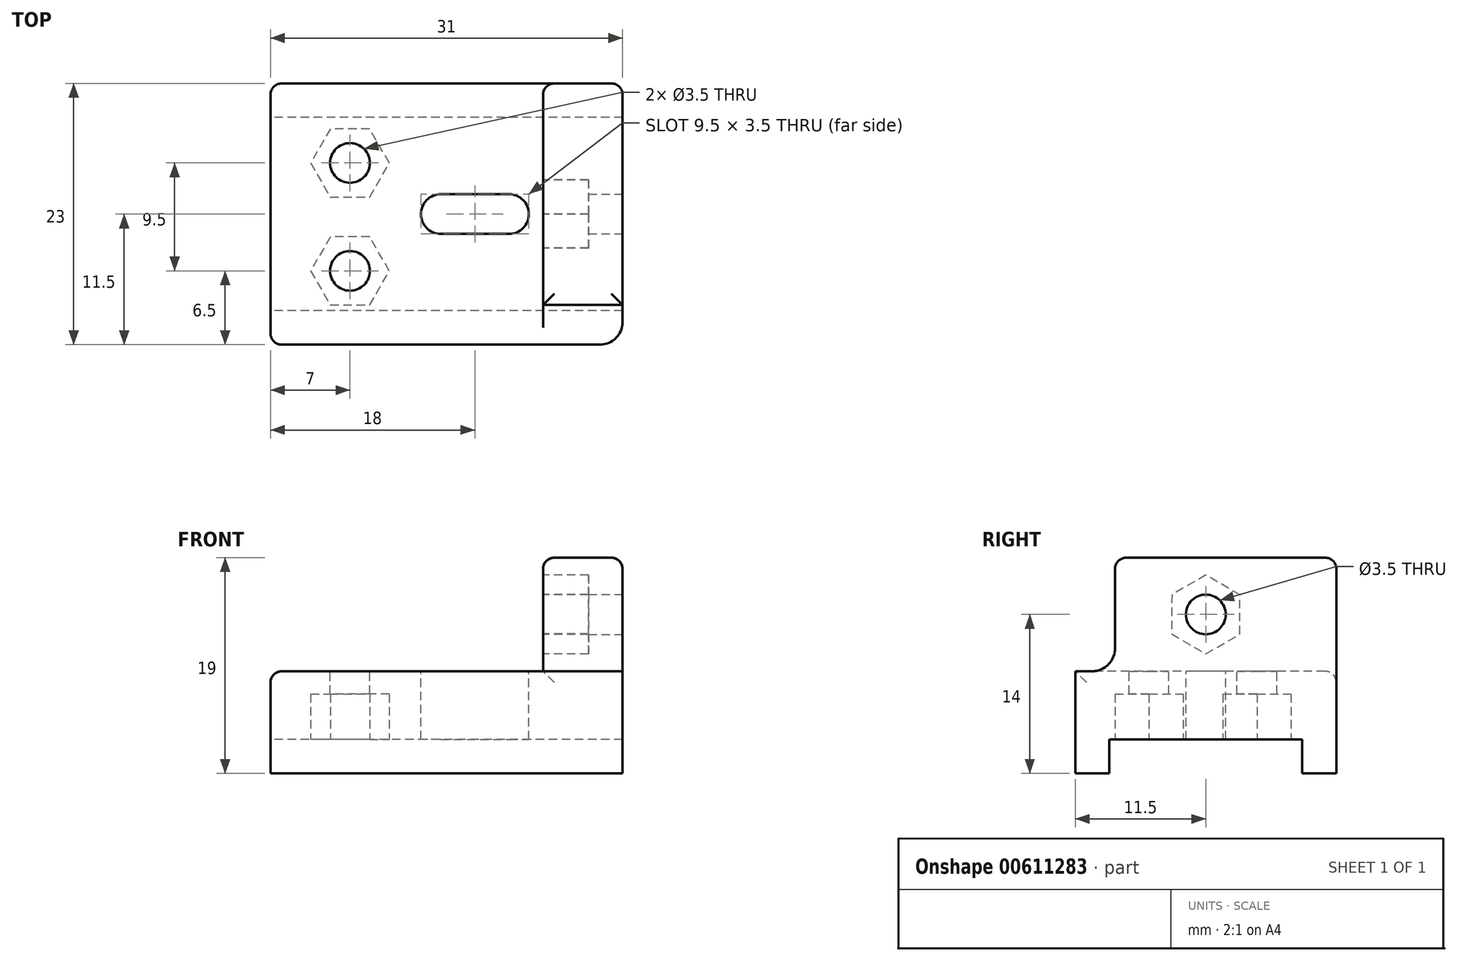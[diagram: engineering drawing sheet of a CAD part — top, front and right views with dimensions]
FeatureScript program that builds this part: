
annotation { "Feature Type Name" : "Feature", "Feature Type Description" : "" }
export const myFeature = defineFeature(function(context is Context, id is Id, definition is map)
    precondition{}
    {
        {
            var Q0;
            Q0=qCreatedBy(makeId("Top.planeOp"),FACE);
            var sketch = newSketch(context, id + "F0", { "sketchPlane" : qUnion([Q0])});
            skLineSegment(sketch, "E0.bottom", {"start": v(0, 0) * mm, "end": v(14, 0) * mm});
            skLineSegment(sketch, "E0.top", {"start": v(0, -23) * mm, "end": v(14, -23) * mm});
            skLineSegment(sketch, "E0.left", {"start": v(0, 0) * mm, "end": v(0, -23) * mm});
            skLineSegment(sketch, "E0.right", {"start": v(14, 0) * mm, "end": v(14, -23) * mm});
            skLineSegment(sketch, "E1.bottom", {"start": v(0, -7) * mm, "end": v(14, -7) * mm, "construction": true});
            skLineSegment(sketch, "E1.top", {"start": v(0, -16.5) * mm, "end": v(14, -16.5) * mm, "construction": true});
            skLineSegment(sketch, "E1.left", {"start": v(0, -7) * mm, "end": v(0, -16.5) * mm, "construction": true});
            skLineSegment(sketch, "E1.right", {"start": v(14, -7) * mm, "end": v(14, -16.5) * mm, "construction": true});
            skCircle(sketch, "E2", {"center": v(7, -7) * mm, "radius": 1.75 * mm});
            skCircle(sketch, "E3", {"center": v(7, -16.5) * mm, "radius": 1.75 * mm});
            skSolve(sketch);
        }
        {
            var Q0;
            Q0=makeQuery(id+"F0.imprint","IMPRINT",FACE,{"disambiguationData":[TD([[makeQuery(id+"F0.imprint","IMPRINT",EDGE,{"derivedFrom":sQuery(id+"F0.wireOp",EDGE,"E0.bottom")}),-1.0]])]});
            var Q1;
            Q1=makeQuery(id+"F0.imprint","IMPRINT",FACE,{"disambiguationData":[TD([[makeQuery(id+"F0.imprint","IMPRINT",EDGE,{"derivedFrom":sQuery(id+"F0.wireOp",EDGE,"E2")}),1.0]])]});
            var Q2;
            Q2=makeQuery(id+"F0.imprint","IMPRINT",FACE,{"disambiguationData":[TD([[makeQuery(id+"F0.imprint","IMPRINT",EDGE,{"derivedFrom":sQuery(id+"F0.wireOp",EDGE,"E3")}),1.0]])]});
            extrude(context, id + "F1", {"entities" : qUnion([Q0, Q1, Q2]), "depth" : 6 * mm, "offsetDistance" : 25 * mm});
        }
        {
            var Q0;
            Q0=makeQuery(id+"F1.opExtrude","CAP_FACE",FACE,{"disambiguationData":[OSD([sQuery(id+"F0.wireOp",EDGE,"E0.bottom"),sQuery(id+"F0.wireOp",EDGE,"E0.top"),sQuery(id+"F0.wireOp",EDGE,"E0.left"),sQuery(id+"F0.wireOp",EDGE,"E0.right")])],"isStart":true});
            var sketch = newSketch(context, id + "F2", { "sketchPlane" : qUnion([Q0])});
            skLineSegment(sketch, "E4.bottom", {"start": v(14, 7) * mm, "end": v(0, 7) * mm, "construction": true});
            skLineSegment(sketch, "E4.top", {"start": v(14, 16.5) * mm, "end": v(0, 16.5) * mm, "construction": true});
            skLineSegment(sketch, "E4.left", {"start": v(14, 7) * mm, "end": v(14, 16.5) * mm, "construction": true});
            skLineSegment(sketch, "E4.right", {"start": v(0, 7) * mm, "end": v(0, 16.5) * mm, "construction": true});
            skCircle(sketch, "E5.cCircle", {"center": v(7, 7) * mm, "radius": 3 * mm, "construction": true});
            skLineSegment(sketch, "E5.0", {"start": v(8.73, 4) * mm, "end": v(5.27, 4) * mm});
            skLineSegment(sketch, "E5.1", {"start": v(5.27, 4) * mm, "end": v(3.54, 7) * mm});
            skLineSegment(sketch, "E5.2", {"start": v(3.54, 7) * mm, "end": v(5.27, 10) * mm});
            skLineSegment(sketch, "E5.3", {"start": v(5.27, 10) * mm, "end": v(8.73, 10) * mm});
            skLineSegment(sketch, "E5.4", {"start": v(8.73, 10) * mm, "end": v(10.46, 7) * mm});
            skLineSegment(sketch, "E5.5", {"start": v(10.46, 7) * mm, "end": v(8.73, 4) * mm});
            skPoint(sketch, "E5.0.midPoint", {"position": v(7, 4) * mm});
            skCircle(sketch, "E6.cCircle", {"center": v(7, 16.5) * mm, "radius": 3 * mm, "construction": true});
            skLineSegment(sketch, "E6.0", {"start": v(8.73, 13.5) * mm, "end": v(5.27, 13.5) * mm});
            skLineSegment(sketch, "E6.1", {"start": v(5.27, 13.5) * mm, "end": v(3.54, 16.5) * mm});
            skLineSegment(sketch, "E6.2", {"start": v(3.54, 16.5) * mm, "end": v(5.27, 19.5) * mm});
            skLineSegment(sketch, "E6.3", {"start": v(5.27, 19.5) * mm, "end": v(8.73, 19.5) * mm});
            skLineSegment(sketch, "E6.4", {"start": v(8.73, 19.5) * mm, "end": v(10.46, 16.5) * mm});
            skLineSegment(sketch, "E6.5", {"start": v(10.46, 16.5) * mm, "end": v(8.73, 13.5) * mm});
            skPoint(sketch, "E6.0.midPoint", {"position": v(7, 13.5) * mm});
            skSolve(sketch);
        }
        {
            var Q0;
            Q0=makeQuery(id+"F2.imprint","IMPRINT",FACE,{"disambiguationData":[TD([[makeQuery(id+"F2.imprint","IMPRINT",EDGE,{"derivedFrom":sQuery(id+"F2.wireOp",EDGE,"E5.0")}),-1.0]])]});
            var Q1;
            Q1=makeQuery(id+"F2.imprint","IMPRINT",FACE,{"disambiguationData":[TD([[makeQuery(id+"F2.imprint","IMPRINT",EDGE,{"derivedFrom":sQuery(id+"F2.wireOp",EDGE,"E6.0")}),-1.0]])]});
            extrude(context, id + "F3", {"entities" : qUnion([Q0, Q1]), "operationType" : NewBodyOperationType.REMOVE, "oppositeDirection" : true, "depth" : 4 * mm, "offsetDistance" : 25 * mm});
        }
        {
            var Q0;
            Q0=makeQuery(id+"F1.opExtrude","CAP_FACE",FACE,{"disambiguationData":[OSD([sQuery(id+"F0.wireOp",EDGE,"E0.bottom"),sQuery(id+"F0.wireOp",EDGE,"E0.top"),sQuery(id+"F0.wireOp",EDGE,"E0.left"),sQuery(id+"F0.wireOp",EDGE,"E0.right")])],"isStart":false});
            var sketch = newSketch(context, id + "F4", { "sketchPlane" : qUnion([Q0])});
            skLineSegment(sketch, "E7.bottom", {"start": v(0, -7) * mm, "end": v(14, -7) * mm, "construction": true});
            skLineSegment(sketch, "E7.top", {"start": v(0, -16.5) * mm, "end": v(14, -16.5) * mm, "construction": true});
            skLineSegment(sketch, "E7.left", {"start": v(0, -7) * mm, "end": v(0, -16.5) * mm, "construction": true});
            skLineSegment(sketch, "E7.right", {"start": v(14, -7) * mm, "end": v(14, -16.5) * mm, "construction": true});
            skCircle(sketch, "E8", {"center": v(7, -7) * mm, "radius": 1.75 * mm});
            skCircle(sketch, "E9", {"center": v(7, -16.5) * mm, "radius": 1.75 * mm});
            skSolve(sketch);
        }
        {
            var Q0;
            Q0=makeQuery(id+"F4.imprint","IMPRINT",FACE,{"disambiguationData":[TD([[makeQuery(id+"F4.imprint","IMPRINT",EDGE,{"derivedFrom":sQuery(id+"F4.wireOp",EDGE,"E8")}),1.0]])]});
            var Q1;
            Q1=makeQuery(id+"F4.imprint","IMPRINT",FACE,{"disambiguationData":[TD([[makeQuery(id+"F4.imprint","IMPRINT",EDGE,{"derivedFrom":sQuery(id+"F4.wireOp",EDGE,"E9")}),1.0]])]});
            extrude(context, id + "F5", {"entities" : qUnion([Q0, Q1]), "operationType" : NewBodyOperationType.REMOVE, "oppositeDirection" : true, "depth" : 25 * mm, "offsetDistance" : 25 * mm});
        }
        {
            var Q0;
            Q0=makeQuery(id+"F1.opExtrude","CAP_FACE",FACE,{"disambiguationData":[OSD([sQuery(id+"F0.wireOp",EDGE,"E0.bottom"),sQuery(id+"F0.wireOp",EDGE,"E0.top"),sQuery(id+"F0.wireOp",EDGE,"E0.left"),sQuery(id+"F0.wireOp",EDGE,"E0.right")])],"isStart":true});
            var sketch = newSketch(context, id + "F6", { "sketchPlane" : qUnion([Q0])});
            skLineSegment(sketch, "E10.bottom", {"start": v(14, 3) * mm, "end": v(0, 3) * mm});
            skLineSegment(sketch, "E10.top", {"start": v(14, 0) * mm, "end": v(0, 0) * mm});
            skLineSegment(sketch, "E10.left", {"start": v(14, 3) * mm, "end": v(14, 0) * mm});
            skLineSegment(sketch, "E10.right", {"start": v(0, 3) * mm, "end": v(0, 0) * mm});
            skLineSegment(sketch, "E11.bottom", {"start": v(14, 23) * mm, "end": v(0, 23) * mm});
            skLineSegment(sketch, "E11.top", {"start": v(14, 20) * mm, "end": v(0, 20) * mm});
            skLineSegment(sketch, "E11.left", {"start": v(14, 23) * mm, "end": v(14, 20) * mm});
            skLineSegment(sketch, "E11.right", {"start": v(0, 23) * mm, "end": v(0, 20) * mm});
            skSolve(sketch);
        }
        {
            var Q0;
            Q0=makeQuery(id+"F6.imprint","IMPRINT",FACE,{"disambiguationData":[TD([[makeQuery(id+"F6.imprint","IMPRINT",EDGE,{"derivedFrom":sQuery(id+"F6.wireOp",EDGE,"E10.bottom")}),1.0]])]});
            var Q1;
            Q1=makeQuery(id+"F6.imprint","IMPRINT",FACE,{"disambiguationData":[TD([[makeQuery(id+"F6.imprint","IMPRINT",EDGE,{"derivedFrom":sQuery(id+"F6.wireOp",EDGE,"E11.bottom")}),-1.0]])]});
            extrude(context, id + "F7", {"entities" : qUnion([Q0, Q1]), "operationType" : NewBodyOperationType.ADD, "depth" : 3 * mm, "offsetDistance" : 25 * mm});
        }
        {
            var Q0;
            Q0=makeQuery(id+"F7.boolean.opBoolean","MERGE",FACE,{"derivedFrom":[makeQuery(id+"F1.opExtrude","SWEPT_FACE",FACE,{"disambiguationData":[OSD([sQuery(id+"F0.wireOp",EDGE,"E0.right")])]}),makeQuery(id+"F7.opExtrude","SWEPT_FACE",FACE,{"disambiguationData":[OSD([sQuery(id+"F6.wireOp",EDGE,"E10.left")])]}),makeQuery(id+"F7.opExtrude","SWEPT_FACE",FACE,{"disambiguationData":[OSD([sQuery(id+"F6.wireOp",EDGE,"E11.left")])]})]});
            extrude(context, id + "F8", {"entities" : qUnion([Q0]), "operationType" : NewBodyOperationType.ADD, "depth" : 17 * mm, "offsetDistance" : 25 * mm});
        }
        {
            var Q0;
            {var subQ0=sQuery(id+"F0.wireOp",EDGE,"E0.right");Q0=makeQuery(id+"F8.boolean.opBoolean","MERGE",FACE,{"derivedFrom":[makeQuery(id+"F1.opExtrude","CAP_FACE",FACE,{"disambiguationData":[OSD([sQuery(id+"F0.wireOp",EDGE,"E0.bottom"),sQuery(id+"F0.wireOp",EDGE,"E0.top"),sQuery(id+"F0.wireOp",EDGE,"E0.left"),subQ0])],"isStart":false}),makeQuery(id+"F8.opExtrude","SWEPT_FACE",FACE,{"disambiguationData":[OSD([subQ0]),TDD([makeQuery(id+"F1.opExtrude","CAP_EDGE",EDGE,{"disambiguationData":[OSD([subQ0])],"isStart":false})])]})]});}
            var sketch = newSketch(context, id + "F9", { "sketchPlane" : qUnion([Q0])});
            skLineSegment(sketch, "E12.bottom", {"start": v(24, 0) * mm, "end": v(31, 0) * mm});
            skLineSegment(sketch, "E12.top", {"start": v(24, -23) * mm, "end": v(31, -23) * mm});
            skLineSegment(sketch, "E12.left", {"start": v(24, 0) * mm, "end": v(24, -23) * mm});
            skLineSegment(sketch, "E12.right", {"start": v(31, 0) * mm, "end": v(31, -23) * mm});
            skSolve(sketch);
        }
        {
            var Q0;
            Q0=makeQuery(id+"F9.imprint","IMPRINT",FACE,{"disambiguationData":[TD([[makeQuery(id+"F9.imprint","IMPRINT",EDGE,{"derivedFrom":sQuery(id+"F9.wireOp",EDGE,"E12.bottom")}),-1.0]])]});
            extrude(context, id + "F10", {"entities" : qUnion([Q0]), "operationType" : NewBodyOperationType.ADD, "depth" : 10 * mm, "offsetDistance" : 25 * mm});
        }
        {
            var Q0;
            Q0=makeQuery(id+"F10.opExtrude","SWEPT_FACE",FACE,{"disambiguationData":[OSD([sQuery(id+"F9.wireOp",EDGE,"E12.left")])]});
            var sketch = newSketch(context, id + "F11", { "sketchPlane" : qUnion([Q0])});
            skLineSegment(sketch, "E13", {"start": v(0, 11) * mm, "end": v(23, 11) * mm, "construction": true});
            skCircle(sketch, "E14.cCircle", {"center": v(11.5, 11) * mm, "radius": 3 * mm, "construction": true});
            skLineSegment(sketch, "E14.0", {"start": v(8.49, 12.71) * mm, "end": v(11.48, 14.46) * mm});
            skLineSegment(sketch, "E14.1", {"start": v(11.48, 14.46) * mm, "end": v(14.49, 12.75) * mm});
            skLineSegment(sketch, "E14.2", {"start": v(14.49, 12.75) * mm, "end": v(14.51, 9.29) * mm});
            skLineSegment(sketch, "E14.3", {"start": v(14.51, 9.29) * mm, "end": v(11.52, 7.54) * mm});
            skLineSegment(sketch, "E14.4", {"start": v(11.52, 7.54) * mm, "end": v(8.51, 9.25) * mm});
            skLineSegment(sketch, "E14.5", {"start": v(8.51, 9.25) * mm, "end": v(8.49, 12.71) * mm});
            skPoint(sketch, "E14.0.midPoint", {"position": v(9.98, 13.59) * mm});
            skSolve(sketch);
        }
        {
            var Q0;
            Q0=makeQuery(id+"F11.imprint","IMPRINT",FACE,{"disambiguationData":[TD([[makeQuery(id+"F11.imprint","IMPRINT",EDGE,{"derivedFrom":sQuery(id+"F11.wireOp",EDGE,"E14.0")}),-1.0]])]});
            extrude(context, id + "F12", {"entities" : qUnion([Q0]), "operationType" : NewBodyOperationType.REMOVE, "oppositeDirection" : true, "depth" : 4 * mm, "offsetDistance" : 25 * mm});
        }
        {
            var Q0;
            Q0=makeQuery(id+"F10.boolean.opBoolean","MERGE",FACE,{"derivedFrom":[makeQuery(id+"F8.opExtrude","CAP_FACE",FACE,{"disambiguationData":[OSD([sQuery(id+"F0.wireOp",EDGE,"E0.right"),sQuery(id+"F6.wireOp",EDGE,"E10.left"),sQuery(id+"F6.wireOp",EDGE,"E11.left")])],"isStart":false}),makeQuery(id+"F10.opExtrude","SWEPT_FACE",FACE,{"disambiguationData":[OSD([sQuery(id+"F9.wireOp",EDGE,"E12.right")])]})]});
            var sketch = newSketch(context, id + "F13", { "sketchPlane" : qUnion([Q0])});
            skLineSegment(sketch, "E15", {"start": v(0, 11) * mm, "end": v(-23, 11) * mm, "construction": true});
            skCircle(sketch, "E16", {"center": v(-11.5, 11) * mm, "radius": 1.75 * mm});
            skSolve(sketch);
        }
        {
            var Q0;
            Q0=makeQuery(id+"F13.imprint","IMPRINT",FACE,{"disambiguationData":[TD([[makeQuery(id+"F13.imprint","IMPRINT",EDGE,{"derivedFrom":sQuery(id+"F13.wireOp",EDGE,"E16")}),1.0]])]});
            extrude(context, id + "F14", {"entities" : qUnion([Q0]), "operationType" : NewBodyOperationType.REMOVE, "oppositeDirection" : true, "depth" : 25 * mm, "offsetDistance" : 25 * mm});
        }
        {
            var Q0;
            {var subQ0=sQuery(id+"F0.wireOp",EDGE,"E0.right");Q0=makeQuery(id+"F8.boolean.opBoolean","MERGE",FACE,{"derivedFrom":[makeQuery(id+"F1.opExtrude","CAP_FACE",FACE,{"disambiguationData":[OSD([sQuery(id+"F0.wireOp",EDGE,"E0.bottom"),sQuery(id+"F0.wireOp",EDGE,"E0.top"),sQuery(id+"F0.wireOp",EDGE,"E0.left"),subQ0])],"isStart":false}),makeQuery(id+"F8.opExtrude","SWEPT_FACE",FACE,{"disambiguationData":[OSD([subQ0]),TDD([makeQuery(id+"F1.opExtrude","CAP_EDGE",EDGE,{"disambiguationData":[OSD([subQ0])],"isStart":false})])]})]});}
            var sketch = newSketch(context, id + "F15", { "sketchPlane" : qUnion([Q0])});
            skLineSegment(sketch, "E17", {"start": v(21, 0) * mm, "end": v(21, -23) * mm, "construction": true});
            skCircle(sketch, "E18", {"center": v(21, -11.5) * mm, "radius": 1.75 * mm});
            skLineSegment(sketch, "E19", {"start": v(14, 0) * mm, "end": v(14, -23) * mm, "construction": true});
            skLineSegment(sketch, "E20", {"start": v(15, 0) * mm, "end": v(15, -23) * mm, "construction": true});
            skCircle(sketch, "E21", {"center": v(15, -11.5) * mm, "radius": 1.75 * mm});
            skLineSegment(sketch, "E22", {"start": v(15, -9.75) * mm, "end": v(21, -9.75) * mm});
            skLineSegment(sketch, "E23", {"start": v(15, -13.25) * mm, "end": v(21, -13.25) * mm});
            skSolve(sketch);
        }
        {
            var Q0;
            {var subQ0=sQuery(id+"F15.wireOp",EDGE,"E22");Q0=makeQuery(id+"F15.imprint","IMPRINT",FACE,{"disambiguationData":[TD([[makeQuery(id+"F15.imprint","IMPRINT",EDGE,{"derivedFrom":subQ0}),-1.0]])]});}
            var Q1;
            {var subQ0=sQuery(id+"F15.wireOp",EDGE,"E21");var subQ1=makeQuery(id+"F15.imprint","INTERSECT",VERTEX,{"derivedFrom":[subQ0,sQuery(id+"F15.wireOp",EDGE,"E22")]});Q1=makeQuery(id+"F15.imprint","IMPRINT",FACE,{"disambiguationData":[TD([[makeQuery(id+"F15.imprint","IMPRINT",EDGE,{"disambiguationData":[TD([[subQ1,-1.0]])],"derivedFrom":subQ0}),1.0]])]});}
            var Q2;
            {var subQ0=sQuery(id+"F15.wireOp",EDGE,"E18");var subQ1=makeQuery(id+"F15.imprint","INTERSECT",VERTEX,{"derivedFrom":[subQ0,sQuery(id+"F15.wireOp",EDGE,"E22")]});Q2=makeQuery(id+"F15.imprint","IMPRINT",FACE,{"disambiguationData":[TD([[makeQuery(id+"F15.imprint","IMPRINT",EDGE,{"disambiguationData":[TD([[subQ1,-1.0]])],"derivedFrom":subQ0}),1.0]])]});}
            extrude(context, id + "F16", {"entities" : qUnion([Q0, Q1, Q2]), "operationType" : NewBodyOperationType.REMOVE, "oppositeDirection" : true, "depth" : 25 * mm, "offsetDistance" : 25 * mm});
        }
        {
            var Q0;
            {var subQ0=sQuery(id+"F6.wireOp",EDGE,"E11.bottom");var subQ1=sQuery(id+"F0.wireOp",EDGE,"E0.top");Q0=makeQuery(id+"F10.boolean.opBoolean","MERGE",FACE,{"derivedFrom":[makeQuery(id+"F8.boolean.opBoolean","MERGE",FACE,{"derivedFrom":[makeQuery(id+"F7.boolean.opBoolean","MERGE",FACE,{"derivedFrom":[makeQuery(id+"F1.opExtrude","SWEPT_FACE",FACE,{"disambiguationData":[OSD([subQ1])]}),makeQuery(id+"F7.opExtrude","SWEPT_FACE",FACE,{"disambiguationData":[OSD([subQ0])]})]}),makeQuery(id+"F8.opExtrude","SWEPT_FACE",FACE,{"disambiguationData":[OSD([subQ1,sQuery(id+"F0.wireOp",EDGE,"E0.right"),subQ0,sQuery(id+"F6.wireOp",EDGE,"E11.left")])]})]}),makeQuery(id+"F10.opExtrude","SWEPT_FACE",FACE,{"disambiguationData":[OSD([sQuery(id+"F9.wireOp",EDGE,"E12.top")])]})]});}
            var sketch = newSketch(context, id + "F17", { "sketchPlane" : qUnion([Q0])});
            skLineSegment(sketch, "E24.bottom", {"start": v(24, 6) * mm, "end": v(31, 6) * mm});
            skLineSegment(sketch, "E24.top", {"start": v(24, 16) * mm, "end": v(31, 16) * mm});
            skLineSegment(sketch, "E24.left", {"start": v(24, 6) * mm, "end": v(24, 16) * mm});
            skLineSegment(sketch, "E24.right", {"start": v(31, 6) * mm, "end": v(31, 16) * mm});
            skSolve(sketch);
        }
        {
            var Q0;
            Q0=makeQuery(id+"F17.imprint","IMPRINT",FACE,{"disambiguationData":[TD([[makeQuery(id+"F17.imprint","IMPRINT",EDGE,{"derivedFrom":sQuery(id+"F17.wireOp",EDGE,"E24.bottom")}),1.0]])]});
            extrude(context, id + "F18", {"entities" : qUnion([Q0]), "operationType" : NewBodyOperationType.REMOVE, "oppositeDirection" : true, "depth" : 3.5 * mm, "offsetDistance" : 25 * mm});
        }
        {
            var Q0;
            Q0=makeQuery(id+"F10.boolean.opBoolean","MERGE",EDGE,{"derivedFrom":[makeQuery(id+"F8.opExtrude","CAP_EDGE",EDGE,{"disambiguationData":[OSD([sQuery(id+"F0.wireOp",EDGE,"E0.top"),sQuery(id+"F0.wireOp",EDGE,"E0.right"),sQuery(id+"F6.wireOp",EDGE,"E11.bottom"),sQuery(id+"F6.wireOp",EDGE,"E11.left")])],"isStart":false}),makeQuery(id+"F10.opExtrude","SWEPT_EDGE",EDGE,{"disambiguationData":[OSD([sQuery(id+"F9.wireOp",EDGE,"E12.top"),sQuery(id+"F9.wireOp",EDGE,"E12.right")])]})]});
            fillet(context, id + "F19", {"entities" : qUnion([Q0]), "radius" : 2 * mm, "tangentPropagation" : true, "allowEdgeOverflow" : false});
        }
        {
            var Q0;
            Q0=makeQuery(id+"F18.boolean.opBoolean","COPY",EDGE,{"derivedFrom":makeQuery(id+"F18.opExtrude","CAP_EDGE",EDGE,{"disambiguationData":[OSD([sQuery(id+"F17.wireOp",EDGE,"E24.bottom")])],"isStart":false})});
            fillet(context, id + "F20", {"entities" : qUnion([Q0]), "radius" : 2 * mm, "tangentPropagation" : true, "allowEdgeOverflow" : false});
        }
        {
            var Q0;
            Q0=makeQuery(id+"F10.opExtrude","CAP_FACE",FACE,{"disambiguationData":[OSD([sQuery(id+"F9.wireOp",EDGE,"E12.bottom"),sQuery(id+"F9.wireOp",EDGE,"E12.top"),sQuery(id+"F9.wireOp",EDGE,"E12.left"),sQuery(id+"F9.wireOp",EDGE,"E12.right")])],"isStart":false});
            var Q1;
            Q1=makeQuery(id+"F10.boolean.opBoolean","MERGE",EDGE,{"derivedFrom":[makeQuery(id+"F8.opExtrude","CAP_EDGE",EDGE,{"disambiguationData":[OSD([sQuery(id+"F0.wireOp",EDGE,"E0.bottom"),sQuery(id+"F0.wireOp",EDGE,"E0.right"),sQuery(id+"F6.wireOp",EDGE,"E10.top"),sQuery(id+"F6.wireOp",EDGE,"E10.left")])],"isStart":false}),makeQuery(id+"F10.opExtrude","SWEPT_EDGE",EDGE,{"disambiguationData":[OSD([sQuery(id+"F9.wireOp",EDGE,"E12.bottom"),sQuery(id+"F9.wireOp",EDGE,"E12.right")])]})]});
            var Q2;
            Q2=makeQuery(id+"F10.opExtrude","SWEPT_EDGE",EDGE,{"disambiguationData":[OSD([sQuery(id+"F0.wireOp",EDGE,"E0.bottom"),sQuery(id+"F0.wireOp",EDGE,"E0.right"),sQuery(id+"F9.wireOp",EDGE,"E12.bottom"),sQuery(id+"F9.wireOp",EDGE,"E12.left")])]});
            var Q3;
            {var subQ0=sQuery(id+"F0.wireOp",EDGE,"E0.bottom");Q3=makeQuery(id+"F8.boolean.opBoolean","MERGE",EDGE,{"derivedFrom":[makeQuery(id+"F1.opExtrude","CAP_EDGE",EDGE,{"disambiguationData":[OSD([subQ0])],"isStart":false}),makeQuery(id+"F8.opExtrude","SWEPT_EDGE",EDGE,{"disambiguationData":[OSD([subQ0,sQuery(id+"F0.wireOp",EDGE,"E0.right")])]})]});}
            var Q4;
            Q4=makeQuery(id+"F10.opExtrude","CAP_EDGE",EDGE,{"disambiguationData":[OSD([sQuery(id+"F9.wireOp",EDGE,"E12.left")])],"isStart":true});
            var Q5;
            Q5=makeQuery(id+"F18.boolean.opBoolean","COPY",EDGE,{"derivedFrom":makeQuery(id+"F18.opExtrude","CAP_EDGE",EDGE,{"disambiguationData":[OSD([sQuery(id+"F17.wireOp",EDGE,"E24.left")])],"isStart":false})});
            var Q6;
            Q6=makeQuery(id+"F18.boolean.opBoolean","COPY",EDGE,{"derivedFrom":makeQuery(id+"F18.opExtrude","CAP_EDGE",EDGE,{"disambiguationData":[OSD([sQuery(id+"F17.wireOp",EDGE,"E24.right")])],"isStart":false})});
            var Q7;
            Q7=makeQuery(id+"F1.opExtrude","CAP_EDGE",EDGE,{"disambiguationData":[OSD([sQuery(id+"F0.wireOp",EDGE,"E0.left")])],"isStart":false});
            var Q8;
            Q8=makeQuery(id+"F7.boolean.opBoolean","MERGE",EDGE,{"derivedFrom":[makeQuery(id+"F1.opExtrude","SWEPT_EDGE",EDGE,{"disambiguationData":[OSD([sQuery(id+"F0.wireOp",EDGE,"E0.top"),sQuery(id+"F0.wireOp",EDGE,"E0.left")])]}),makeQuery(id+"F7.opExtrude","SWEPT_EDGE",EDGE,{"disambiguationData":[OSD([sQuery(id+"F6.wireOp",EDGE,"E11.bottom"),sQuery(id+"F6.wireOp",EDGE,"E11.right")])]})]});
            var Q9;
            Q9=makeQuery(id+"F7.boolean.opBoolean","MERGE",EDGE,{"derivedFrom":[makeQuery(id+"F1.opExtrude","SWEPT_EDGE",EDGE,{"disambiguationData":[OSD([sQuery(id+"F0.wireOp",EDGE,"E0.bottom"),sQuery(id+"F0.wireOp",EDGE,"E0.left")])]}),makeQuery(id+"F7.opExtrude","SWEPT_EDGE",EDGE,{"disambiguationData":[OSD([sQuery(id+"F6.wireOp",EDGE,"E10.top"),sQuery(id+"F6.wireOp",EDGE,"E10.right")])]})]});
            fillet(context, id + "F21", {"entities" : qUnion([Q0, Q1, Q2, Q3, Q4, Q5, Q6, Q7, Q8, Q9]), "radius" : 1 * mm, "tangentPropagation" : true, "allowEdgeOverflow" : false});
        }
    });
